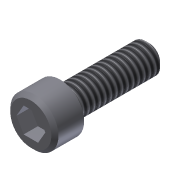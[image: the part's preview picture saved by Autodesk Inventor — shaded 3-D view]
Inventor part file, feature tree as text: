
AUTODESK INVENTOR PART (.ipt)
format: ipt  version: 2013 (Build 170138000, 138)  size: 108,544 bytes
history: native  units: in
note: dims shown in document units (in); Inventor stores cm internally (conversion verified against a paired STEP export)
features: extrude x3, sketch x3, chamfer x2, thread x1
ambient origin geometry x8: Origin, YZ Plane, XZ Plane, XY Plane, X Axis, Y Axis, Z Axis, Center Point
bodies: Solid1 (feature_tree)
feature tree (9):
  extrude  "Extrusion1"  Depth=0.164in TaperAngle=0.0deg
  extrude  "Extrusion2"  Depth=0.5in TaperAngle=0.0deg
  extrude  "Extrusion3"  Depth=0.08in TaperAngle=0.0deg
  thread  "Thread1"  [1 undecoded]
  chamfer  "Chamfer1"  [1 undecoded]
  chamfer  "Chamfer2"  [1 undecoded]
  sketch  "Sketch1"  dims[d0=0.27in d1=0.164in d2=0.0in]
  sketch  "Sketch2"  dims[d3=0.164in d4=0.5in d5=0.0in]
  sketch  "Sketch3"  dims[d6=0.1406in d7=0.08in d8=0.0in d9=1.0in d10=0.0in d11=0.02in d12=0.125in d13=45.0deg d14=0.02in d15=0.125in d16=45.0deg]
note: 3 required parameter values undecoded (feature->parameter linkage not recoverable at this tier; creation-order binding heuristic only, values carry confidence <= 0.55)
